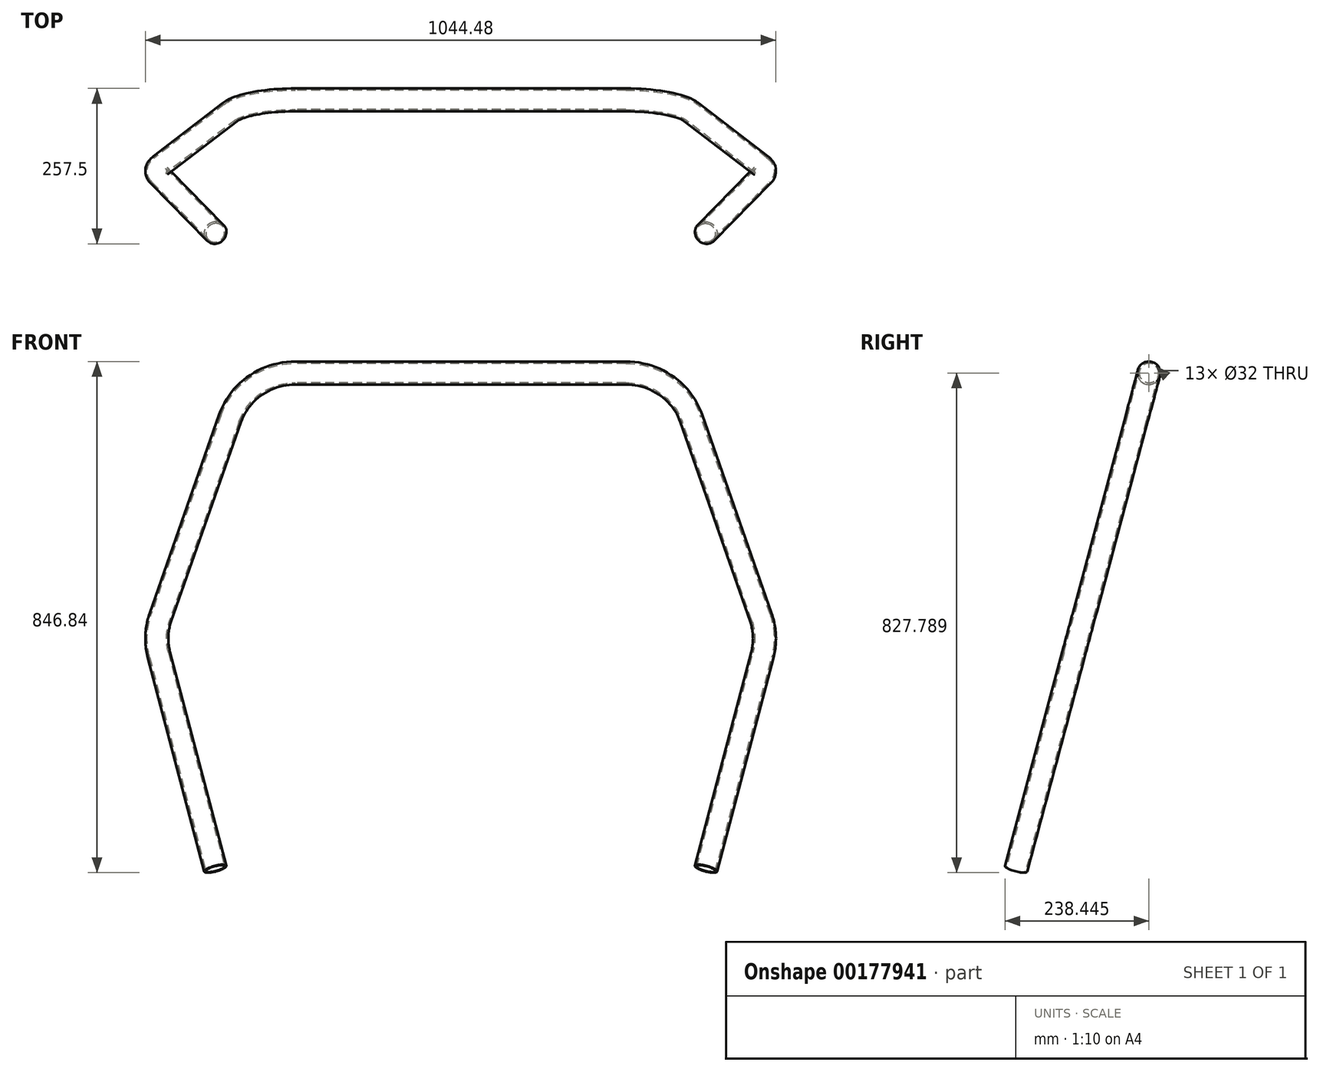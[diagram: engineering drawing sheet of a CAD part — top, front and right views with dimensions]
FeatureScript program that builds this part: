
annotation { "Feature Type Name" : "Feature", "Feature Type Description" : "" }
export const myFeature = defineFeature(function(context is Context, id is Id, definition is map)
    precondition{}
    {
        {
            var Q0;
            Q0=qCreatedBy(makeId("Front.planeOp"),FACE);
            var sketch = newSketch(context, id + "F0", { "sketchPlane" : qUnion([Q0])});
            skLineSegment(sketch, "E0", {"start": v(-1248.36, -254) * mm, "end": v(1248.36, -254) * mm});
            skLineSegment(sketch, "E1", {"start": v(0, 0) * mm, "end": v(0, -254) * mm, "construction": true});
            skLineSegment(sketch, "E2.bottom", {"start": v(787.4, -254) * mm, "end": v(533.4, -254) * mm});
            skLineSegment(sketch, "E2.top", {"start": v(787.4, 304.8) * mm, "end": v(533.4, 304.8) * mm});
            skLineSegment(sketch, "E2.left", {"start": v(787.4, -254) * mm, "end": v(787.4, 304.8) * mm});
            skLineSegment(sketch, "E2.right", {"start": v(533.4, -254) * mm, "end": v(533.4, 304.8) * mm});
            skPoint(sketch, "E2.middle", {"position": v(660.4, 25.4) * mm});
            skPoint(sketch, "E3.MirrorP", {"position": v(-660.4, 25.4) * mm});
            skLineSegment(sketch, "E4.MirrorCS", {"start": v(-533.4, -254) * mm, "end": v(-533.4, 304.8) * mm});
            skLineSegment(sketch, "E5.MirrorCS", {"start": v(-787.4, -254) * mm, "end": v(-787.4, 304.8) * mm});
            skLineSegment(sketch, "E6.MirrorCS", {"start": v(-787.4, 304.8) * mm, "end": v(-533.4, 304.8) * mm});
            skLineSegment(sketch, "E7.MirrorCS", {"start": v(-787.4, -254) * mm, "end": v(-533.4, -254) * mm});
            skLineSegment(sketch, "E8.bottom", {"start": v(787.4, -254) * mm, "end": v(482.6, -254) * mm});
            skLineSegment(sketch, "E8.top", {"start": v(787.4, 419.1) * mm, "end": v(482.6, 419.1) * mm});
            skLineSegment(sketch, "E8.left", {"start": v(787.4, -254) * mm, "end": v(787.4, 419.1) * mm});
            skLineSegment(sketch, "E8.right", {"start": v(482.6, -254) * mm, "end": v(482.6, 419.1) * mm});
            skPoint(sketch, "E8.middle", {"position": v(635, 82.55) * mm});
            skPoint(sketch, "E9.MirrorP", {"position": v(-635, 82.55) * mm});
            skLineSegment(sketch, "E10.MirrorCS", {"start": v(-482.6, -254) * mm, "end": v(-482.6, 419.1) * mm});
            skLineSegment(sketch, "E11.MirrorCS", {"start": v(-787.4, -254) * mm, "end": v(-787.4, 419.1) * mm});
            skLineSegment(sketch, "E12.MirrorCS", {"start": v(-787.4, 419.1) * mm, "end": v(-482.6, 419.1) * mm});
            skLineSegment(sketch, "E13.MirrorCS", {"start": v(-787.4, -254) * mm, "end": v(-482.6, -254) * mm});
            skSolve(sketch);
        }
        {
            var Q0;
            Q0=qCreatedBy(makeId("Right.planeOp"),FACE);
            var sketch = newSketch(context, id + "F1", { "sketchPlane" : qUnion([Q0])});
            skLineSegment(sketch, "E14", {"start": v(-885.83, -254) * mm, "end": v(885.83, -254) * mm});
            skCircle(sketch, "E15", {"center": v(-885.83, 25.4) * mm, "radius": 279.4 * mm});
            skCircle(sketch, "E16", {"center": v(885.83, 82.55) * mm, "radius": 336.55 * mm});
            skLineSegment(sketch, "E17", {"start": v(-885.83, -254) * mm, "end": v(-885.83, 304.8) * mm, "construction": true});
            skLineSegment(sketch, "E18", {"start": v(885.83, -254) * mm, "end": v(885.83, 419.1) * mm, "construction": true});
            skLineSegment(sketch, "E19", {"start": v(-1165.23, 25.4) * mm, "end": v(-606.42, 25.4) * mm, "construction": true});
            skLineSegment(sketch, "E20", {"start": v(549.27, 82.55) * mm, "end": v(1222.37, 82.55) * mm, "construction": true});
            skCircle(sketch, "E21", {"center": v(0, 15.88) * mm, "radius": 15.88 * mm});
            skLineSegment(sketch, "E22", {"start": v(105, 15.87) * mm, "end": v(325.02, 836.96) * mm});
            skCircle(sketch, "E23", {"center": v(325.02, 836.96) * mm, "radius": 19.05 * mm});
            skLineSegment(sketch, "E24", {"start": v(105, 15.87) * mm, "end": v(985.88, 15.87) * mm});
            skLineSegment(sketch, "E25", {"start": v(315.25, 800.52) * mm, "end": v(-56.67, 800.52) * mm});
            skLineSegment(sketch, "E26", {"start": v(105, 15.88) * mm, "end": v(-1105.1, 15.87) * mm});
            skLineSegment(sketch, "E27", {"start": v(985.88, 15.87) * mm, "end": v(985.88, 216.69) * mm});
            skLineSegment(sketch, "E28", {"start": v(985.88, 216.69) * mm, "end": v(643, 216.69) * mm});
            skLineSegment(sketch, "E29", {"start": v(643, 216.69) * mm, "end": v(643, 15.87) * mm});
            skLineSegment(sketch, "E30", {"start": v(757.23, 473.22) * mm, "end": v(985.88, 216.69) * mm});
            skLineSegment(sketch, "E31", {"start": v(757.23, 473.22) * mm, "end": v(315.25, 800.52) * mm});
            skLineSegment(sketch, "E32", {"start": v(643, 216.69) * mm, "end": v(757.23, 473.22) * mm});
            skLineSegment(sketch, "E33", {"start": v(207.17, 397.16) * mm, "end": v(643, 216.69) * mm});
            skLineSegment(sketch, "E34", {"start": v(207.17, 397.16) * mm, "end": v(-693.75, 280.72) * mm});
            skLineSegment(sketch, "E35", {"start": v(-693.75, 280.72) * mm, "end": v(-56.67, 800.52) * mm});
            skLineSegment(sketch, "E36", {"start": v(-693.75, 280.72) * mm, "end": v(-1105.1, 280.72) * mm});
            skLineSegment(sketch, "E37", {"start": v(-1105.1, 280.72) * mm, "end": v(-1105.1, 15.87) * mm});
            skLineSegment(sketch, "E38", {"start": v(-693.75, 280.72) * mm, "end": v(-693.75, 15.87) * mm});
            skSolve(sketch);
        }
        {
            var Q0;
            Q0=qCreatedBy(makeId("Top.planeOp"),FACE);
            var Q1;
            Q1=sQuery(id+"F1.wireOp",VERTEX,"E21.center");
            cPlane(context, id + "F2", {"entities" : qUnion([Q0, Q1]), "cplaneType" : CPlaneType.PLANE_POINT, "offset" : 25.4 * mm, "width" : 152.4 * mm, "height" : 152.4 * mm});
        }
        {
            var Q0;
            Q0=qCreatedBy(makeId("Right.planeOp"),FACE);
            var Q1;
            Q1=sQuery(id+"F1.wireOp",EDGE,"E22");
            cPlane(context, id + "F3", {"entities" : qUnion([Q0, Q1]), "cplaneType" : CPlaneType.LINE_ANGLE, "offset" : 25.4 * mm, "angle" : 90 * degree, "width" : 152.4 * mm, "height" : 152.4 * mm});
        }
        {
            var Q0;
            Q0=qCreatedBy(id+"F3.planeOp",FACE);
            var sketch = newSketch(context, id + "F4", { "sketchPlane" : qUnion([Q0])});
            skLineSegment(sketch, "E39", {"start": v(0, 42.51) * mm, "end": v(0, 892.56) * mm, "construction": true});
            skLineSegment(sketch, "E40", {"start": v(0, 892.56) * mm, "end": v(273.6, 892.56) * mm});
            skLineSegment(sketch, "E41", {"start": v(381.87, 814.87) * mm, "end": v(497.17, 473.86) * mm});
            skLineSegment(sketch, "E42", {"start": v(499.66, 409.07) * mm, "end": v(406.4, 42.51) * mm});
            skPoint(sketch, "E43.visualSharp", {"position": v(355.6, 892.56) * mm});
            skArc(sketch, "E43.filletArc", {"start": v(381.87, 814.87) * mm, "mid": v(340.22, 871.13) * mm, "end": v(273.6, 892.56) * mm});
            skPoint(sketch, "E44.visualSharp", {"position": v(508, 441.83) * mm});
            skArc(sketch, "E44.filletArc", {"start": v(499.66, 409.07) * mm, "mid": v(503.1, 441.65) * mm, "end": v(497.17, 473.86) * mm});
            skArc(sketch, "E45.MirrorCS", {"start": v(-499.66, 409.07) * mm, "mid": v(-503.1, 441.65) * mm, "end": v(-497.17, 473.86) * mm});
            skArc(sketch, "E46.MirrorCS", {"start": v(-381.87, 814.87) * mm, "mid": v(-340.22, 871.13) * mm, "end": v(-273.6, 892.56) * mm});
            skLineSegment(sketch, "E47.MirrorCS", {"start": v(0, 892.56) * mm, "end": v(-273.6, 892.56) * mm});
            skPoint(sketch, "E48.MirrorP", {"position": v(-355.6, 892.56) * mm});
            skPoint(sketch, "E49.MirrorP", {"position": v(-508, 441.83) * mm});
            skLineSegment(sketch, "E50.MirrorCS", {"start": v(-499.66, 409.07) * mm, "end": v(-406.4, 42.51) * mm});
            skLineSegment(sketch, "E51.MirrorCS", {"start": v(-381.87, 814.87) * mm, "end": v(-497.17, 473.86) * mm});
            skSolve(sketch);
        }
        {
            var Q0;
            Q0=qCreatedBy(id+"F2.planeOp",FACE);
            var sketch = newSketch(context, id + "F5", { "sketchPlane" : qUnion([Q0])});
            skLineSegment(sketch, "E52", {"start": v(0, 0) * mm, "end": v(0, -1356.72) * mm, "construction": true});
            skLineSegment(sketch, "E53", {"start": v(-222.25, 643) * mm, "end": v(-174.06, 985.88) * mm});
            skLineSegment(sketch, "E54", {"start": v(-228.6, -693.75) * mm, "end": v(-228.6, -1105.1) * mm});
            skLineSegment(sketch, "E55", {"start": v(-228.6, -693.75) * mm, "end": v(228.6, -693.75) * mm});
            skLineSegment(sketch, "E56", {"start": v(-222.25, 643) * mm, "end": v(222.25, 643) * mm});
            skLineSegment(sketch, "E57", {"start": v(-174.06, 985.88) * mm, "end": v(174.06, 985.88) * mm});
            skLineSegment(sketch, "E58.MirrorCS", {"start": v(222.25, 643) * mm, "end": v(174.06, 985.88) * mm});
            skLineSegment(sketch, "E59.MirrorCS", {"start": v(228.6, -693.75) * mm, "end": v(228.6, -1105.1) * mm});
            skLineSegment(sketch, "E60", {"start": v(0, 0) * mm, "end": v(0, 1075.28) * mm, "construction": true});
            skLineSegment(sketch, "E61", {"start": v(-228.6, -693.75) * mm, "end": v(-403.73, 72.83) * mm});
            skLineSegment(sketch, "E62", {"start": v(-400.15, 136.14) * mm, "end": v(-222.25, 643) * mm});
            skPoint(sketch, "E63.visualSharp", {"position": v(-411.08, 105) * mm});
            skArc(sketch, "E63.filletArc", {"start": v(-400.15, 136.14) * mm, "mid": v(-406.42, 104.74) * mm, "end": v(-403.73, 72.83) * mm});
            skLineSegment(sketch, "E64", {"start": v(406.4, 105) * mm, "end": v(-406.4, 105) * mm, "construction": true});
            skLineSegment(sketch, "E65", {"start": v(-228.6, -1105.1) * mm, "end": v(228.6, -1105.1) * mm});
            skLineSegment(sketch, "E66.MirrorCS", {"start": v(400.15, 136.14) * mm, "end": v(222.25, 643) * mm});
            skArc(sketch, "E67.MirrorCS", {"start": v(400.15, 136.14) * mm, "mid": v(406.42, 104.74) * mm, "end": v(403.73, 72.83) * mm});
            skLineSegment(sketch, "E68.MirrorCS", {"start": v(228.6, -693.75) * mm, "end": v(403.73, 72.83) * mm});
            skLineSegment(sketch, "E69", {"start": v(275.26, -489.5) * mm, "end": v(251.93, -696.38) * mm, "construction": true});
            skLineSegment(sketch, "E70", {"start": v(251.93, -696.38) * mm, "end": v(228.6, -693.75) * mm, "construction": true});
            skLineSegment(sketch, "E71", {"start": v(251.93, -696.38) * mm, "end": v(228.6, -903.26) * mm, "construction": true});
            skLineSegment(sketch, "E72", {"start": v(174.06, 985.88) * mm, "end": v(336.92, 316.3) * mm, "construction": true});
            skLineSegment(sketch, "E73", {"start": v(222.25, 643) * mm, "end": v(255.5, 651.08) * mm, "construction": true});
            skSolve(sketch);
        }
        {
            var Q0;
            Q0=sQuery(id+"F4.wireOp",EDGE,"E42");
            var Q1;
            Q1=sQuery(id+"F5.wireOp",VERTEX,"E64.start");
            cPlane(context, id + "F6", {"entities" : qUnion([Q0, Q1]), "cplaneType" : CPlaneType.LINE_POINT, "offset" : 25.4 * mm, "width" : 152.4 * mm, "height" : 152.4 * mm});
        }
        {
            var Q0;
            Q0=qCreatedBy(id+"F6.planeOp",FACE);
            var sketch = newSketch(context, id + "F7", { "sketchPlane" : qUnion([Q0])});
            skCircle(sketch, "E74", {"center": v(383.37, -97.32) * mm, "radius": 19.05 * mm});
            skCircle(sketch, "E75", {"center": v(383.37, -97.32) * mm, "radius": 16 * mm});
            skSolve(sketch);
        }
        {
            var Q0;
            Q0 = qSketchRegion(id + "F7", true);
            var Q1;
            Q1 = qConstructionFilter(qBodyType(qCreatedBy(id + "F4" ,EDGE), BodyType.WIRE), ConstructionObject.NO);
            sweep(context, id + "F8", {"profiles" : qUnion([Q0]), "path" : qUnion([Q1])});
        }
    });
